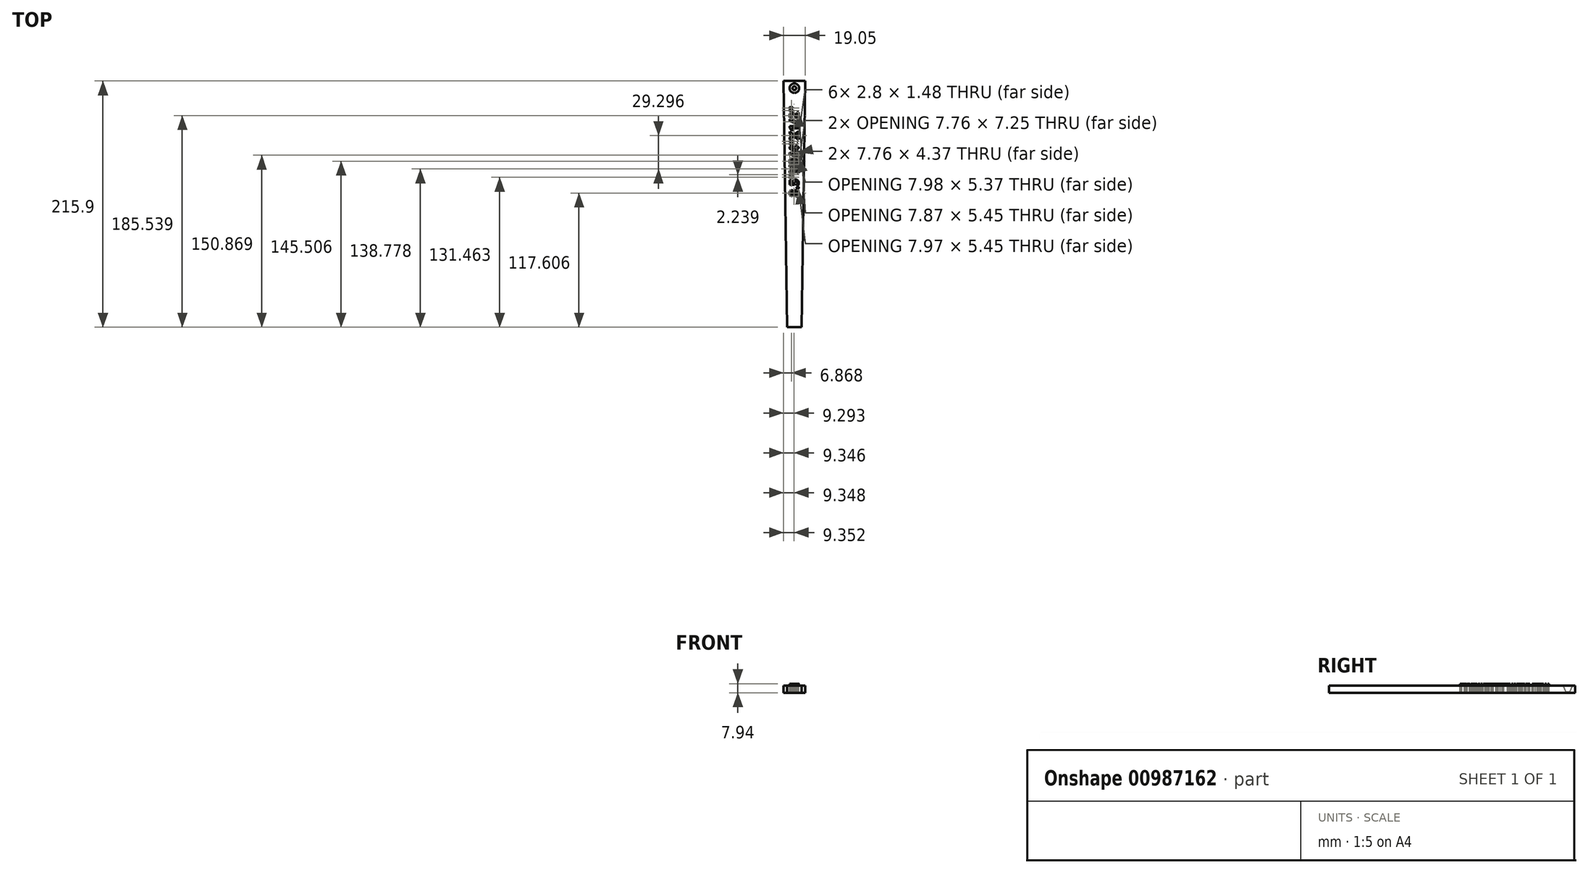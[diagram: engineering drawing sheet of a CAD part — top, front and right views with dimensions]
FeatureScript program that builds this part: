
annotation { "Feature Type Name" : "Feature", "Feature Type Description" : "" }
export const myFeature = defineFeature(function(context is Context, id is Id, definition is map)
    precondition{}
    {
        {
            var Q0;
            Q0=qCreatedBy(makeId("Top.planeOp"),FACE);
            var sketch = newSketch(context, id + "F0", { "sketchPlane" : qUnion([Q0])});
            skLineSegment(sketch, "E0", {"start": v(-44.75, 101.4) * mm, "end": v(-54.28, 101.4) * mm});
            skLineSegment(sketch, "E1", {"start": v(-54.28, 101.4) * mm, "end": v(-44.75, 101.4) * mm});
            skLineSegment(sketch, "E2", {"start": v(-44.75, -114.5) * mm, "end": v(-51.1, -114.5) * mm});
            skLineSegment(sketch, "E3", {"start": v(-51.1, -114.5) * mm, "end": v(-54.28, 101.4) * mm});
            skLineSegment(sketch, "E4.MirrorCS", {"start": v(-44.75, 101.4) * mm, "end": v(-35.23, 101.4) * mm});
            skLineSegment(sketch, "E5.MirrorCS", {"start": v(-38.4, -114.5) * mm, "end": v(-35.23, 101.4) * mm});
            skLineSegment(sketch, "E6.MirrorCS", {"start": v(-44.75, -114.5) * mm, "end": v(-38.4, -114.5) * mm});
            skCircle(sketch, "E7", {"center": v(-44.75, 95.05) * mm, "radius": 1.65 * mm});
            skText(sketch, "E8", { "text": "8.5\"X3/4\"X1/2\"", "fontName": "OpenSans-Bold.ttf"});
            const initialGuessF0  = {"E8": [-0.04105, 0, 0, 1, 0.00783]};
            skSetInitialGuess(sketch, initialGuessF0);
            skSolve(sketch);
        }
        {
            var Q0;
            Q0 = qSketchRegion(id + "F0", true);
            extrude(context, id + "F1", {"entities" : qUnion([Q0]), "oppositeDirection" : true, "depth" : 6.35 * mm, "offsetDistance" : 25.4 * mm});
        }
        {
            var Q0;
            Q0=makeQuery(id+"F0.imprint","IMPRINT",FACE,{"disambiguationData":[TD([[makeQuery(id+"F0.imprint","IMPRINT",EDGE,{"derivedFrom":sQuery(id+"F0.wireOp",EDGE,"E8.sketch_text.stroke-0")}),-1.0]])]});
            var Q1;
            Q1=makeQuery(id+"F0.imprint","IMPRINT",FACE,{"disambiguationData":[TD([[makeQuery(id+"F0.imprint","IMPRINT",EDGE,{"derivedFrom":sQuery(id+"F0.wireOp",EDGE,"E8.sketch_text.stroke-31")}),-1.0]])]});
            var Q2;
            Q2=makeQuery(id+"F0.imprint","IMPRINT",FACE,{"disambiguationData":[TD([[makeQuery(id+"F0.imprint","IMPRINT",EDGE,{"derivedFrom":sQuery(id+"F0.wireOp",EDGE,"E8.sketch_text.stroke-39")}),-1.0]])]});
            var Q3;
            Q3=makeQuery(id+"F0.imprint","IMPRINT",FACE,{"disambiguationData":[TD([[makeQuery(id+"F0.imprint","IMPRINT",EDGE,{"derivedFrom":sQuery(id+"F0.wireOp",EDGE,"E8.sketch_text.stroke-59")}),-1.0]])]});
            var Q4;
            Q4=makeQuery(id+"F0.imprint","IMPRINT",FACE,{"disambiguationData":[TD([[makeQuery(id+"F0.imprint","IMPRINT",EDGE,{"derivedFrom":sQuery(id+"F0.wireOp",EDGE,"E8.sketch_text.stroke-63")}),-1.0]])]});
            var Q5;
            Q5=makeQuery(id+"F0.imprint","IMPRINT",FACE,{"disambiguationData":[TD([[makeQuery(id+"F0.imprint","IMPRINT",EDGE,{"derivedFrom":sQuery(id+"F0.wireOp",EDGE,"E8.sketch_text.stroke-67")}),-1.0]])]});
            var Q6;
            Q6=makeQuery(id+"F0.imprint","IMPRINT",FACE,{"disambiguationData":[TD([[makeQuery(id+"F0.imprint","IMPRINT",EDGE,{"derivedFrom":sQuery(id+"F0.wireOp",EDGE,"E8.sketch_text.stroke-79")}),-1.0]])]});
            var Q7;
            Q7=makeQuery(id+"F0.imprint","IMPRINT",FACE,{"disambiguationData":[TD([[makeQuery(id+"F0.imprint","IMPRINT",EDGE,{"derivedFrom":sQuery(id+"F0.wireOp",EDGE,"E8.sketch_text.stroke-106")}),-1.0]])]});
            var Q8;
            Q8=makeQuery(id+"F0.imprint","IMPRINT",FACE,{"disambiguationData":[TD([[makeQuery(id+"F0.imprint","IMPRINT",EDGE,{"derivedFrom":sQuery(id+"F0.wireOp",EDGE,"E8.sketch_text.stroke-110")}),-1.0]])]});
            var Q9;
            Q9=makeQuery(id+"F0.imprint","IMPRINT",FACE,{"disambiguationData":[TD([[makeQuery(id+"F0.imprint","IMPRINT",EDGE,{"derivedFrom":sQuery(id+"F0.wireOp",EDGE,"E8.sketch_text.stroke-128")}),-1.0]])]});
            var Q10;
            Q10=makeQuery(id+"F0.imprint","IMPRINT",FACE,{"disambiguationData":[TD([[makeQuery(id+"F0.imprint","IMPRINT",EDGE,{"derivedFrom":sQuery(id+"F0.wireOp",EDGE,"E8.sketch_text.stroke-132")}),-1.0]])]});
            var Q11;
            Q11=makeQuery(id+"F0.imprint","IMPRINT",FACE,{"disambiguationData":[TD([[makeQuery(id+"F0.imprint","IMPRINT",EDGE,{"derivedFrom":sQuery(id+"F0.wireOp",EDGE,"E8.sketch_text.stroke-136")}),-1.0]])]});
            var Q12;
            Q12=makeQuery(id+"F0.imprint","IMPRINT",FACE,{"disambiguationData":[TD([[makeQuery(id+"F0.imprint","IMPRINT",EDGE,{"derivedFrom":sQuery(id+"F0.wireOp",EDGE,"E8.sketch_text.stroke-148")}),-1.0]])]});
            var Q13;
            Q13=makeQuery(id+"F0.imprint","IMPRINT",FACE,{"disambiguationData":[TD([[makeQuery(id+"F0.imprint","IMPRINT",EDGE,{"derivedFrom":sQuery(id+"F0.wireOp",EDGE,"E8.sketch_text.stroke-158")}),-1.0]])]});
            var Q14;
            Q14=makeQuery(id+"F0.imprint","IMPRINT",FACE,{"disambiguationData":[TD([[makeQuery(id+"F0.imprint","IMPRINT",EDGE,{"derivedFrom":sQuery(id+"F0.wireOp",EDGE,"E8.sketch_text.stroke-162")}),-1.0]])]});
            var Q15;
            Q15=makeQuery(id+"F0.imprint","IMPRINT",FACE,{"disambiguationData":[TD([[makeQuery(id+"F0.imprint","IMPRINT",EDGE,{"derivedFrom":sQuery(id+"F0.wireOp",EDGE,"E8.sketch_text.stroke-186")}),-1.0]])]});
            var Q16;
            Q16=makeQuery(id+"F0.imprint","IMPRINT",FACE,{"disambiguationData":[TD([[makeQuery(id+"F0.imprint","IMPRINT",EDGE,{"derivedFrom":sQuery(id+"F0.wireOp",EDGE,"E8.sketch_text.stroke-190")}),-1.0]])]});
            extrude(context, id + "F2", {"entities" : qUnion([Q0, Q1, Q2, Q3, Q4, Q5, Q6, Q7, Q8, Q9, Q10, Q11, Q12, Q13, Q14, Q15, Q16]), "depth" : 1.59 * mm, "offsetDistance" : 25.4 * mm});
        }
        {
            var Q0;
            Q0=makeQuery(id+"F1.opExtrude","CAP_EDGE",EDGE,{"disambiguationData":[OSD([sQuery(id+"F0.wireOp",EDGE,"E7")])],"isStart":true});
            chamfer(context, id + "F3", {"entities" : qUnion([Q0]), "chamferType" : ChamferType.TWO_OFFSETS, "width1" : 5.84 * mm, "oppositeDirection" : false, "width2" : 2.54 * mm, "tangentPropagation" : true});
        }
        {
            var Q0;
            Q0=makeQuery(id+"F0.imprint","IMPRINT",FACE,{"disambiguationData":[TD([[makeQuery(id+"F0.imprint","IMPRINT",EDGE,{"derivedFrom":sQuery(id+"F0.wireOp",EDGE,"E8.sketch_text.stroke-23")}),1.0]])]});
            var Q1;
            Q1=makeQuery(id+"F0.imprint","IMPRINT",FACE,{"disambiguationData":[TD([[makeQuery(id+"F0.imprint","IMPRINT",EDGE,{"derivedFrom":sQuery(id+"F0.wireOp",EDGE,"E8.sketch_text.stroke-16")}),1.0]])]});
            var Q2;
            Q2=makeQuery(id+"F0.imprint","IMPRINT",FACE,{"disambiguationData":[TD([[makeQuery(id+"F0.imprint","IMPRINT",EDGE,{"derivedFrom":sQuery(id+"F0.wireOp",EDGE,"E8.sketch_text.stroke-31")}),-1.0]])]});
            var Q3;
            Q3=makeQuery(id+"F0.imprint","IMPRINT",FACE,{"disambiguationData":[TD([[makeQuery(id+"F0.imprint","IMPRINT",EDGE,{"derivedFrom":sQuery(id+"F0.wireOp",EDGE,"E8.sketch_text.stroke-0")}),-1.0]])]});
            var Q4;
            Q4=makeQuery(id+"F0.imprint","IMPRINT",FACE,{"disambiguationData":[TD([[makeQuery(id+"F0.imprint","IMPRINT",EDGE,{"derivedFrom":sQuery(id+"F0.wireOp",EDGE,"E8.sketch_text.stroke-39")}),-1.0]])]});
            var Q5;
            Q5=makeQuery(id+"F0.imprint","IMPRINT",FACE,{"disambiguationData":[TD([[makeQuery(id+"F0.imprint","IMPRINT",EDGE,{"derivedFrom":sQuery(id+"F0.wireOp",EDGE,"E8.sketch_text.stroke-59")}),-1.0]])]});
            var Q6;
            Q6=makeQuery(id+"F0.imprint","IMPRINT",FACE,{"disambiguationData":[TD([[makeQuery(id+"F0.imprint","IMPRINT",EDGE,{"derivedFrom":sQuery(id+"F0.wireOp",EDGE,"E8.sketch_text.stroke-63")}),-1.0]])]});
            var Q7;
            Q7=makeQuery(id+"F0.imprint","IMPRINT",FACE,{"disambiguationData":[TD([[makeQuery(id+"F0.imprint","IMPRINT",EDGE,{"derivedFrom":sQuery(id+"F0.wireOp",EDGE,"E8.sketch_text.stroke-67")}),-1.0]])]});
            var Q8;
            Q8=makeQuery(id+"F0.imprint","IMPRINT",FACE,{"disambiguationData":[TD([[makeQuery(id+"F0.imprint","IMPRINT",EDGE,{"derivedFrom":sQuery(id+"F0.wireOp",EDGE,"E8.sketch_text.stroke-79")}),-1.0]])]});
            var Q9;
            Q9=makeQuery(id+"F0.imprint","IMPRINT",FACE,{"disambiguationData":[TD([[makeQuery(id+"F0.imprint","IMPRINT",EDGE,{"derivedFrom":sQuery(id+"F0.wireOp",EDGE,"E8.sketch_text.stroke-106")}),-1.0]])]});
            var Q10;
            Q10=makeQuery(id+"F0.imprint","IMPRINT",FACE,{"disambiguationData":[TD([[makeQuery(id+"F0.imprint","IMPRINT",EDGE,{"derivedFrom":sQuery(id+"F0.wireOp",EDGE,"E8.sketch_text.stroke-110")}),-1.0]])]});
            var Q11;
            Q11=makeQuery(id+"F0.imprint","IMPRINT",FACE,{"disambiguationData":[TD([[makeQuery(id+"F0.imprint","IMPRINT",EDGE,{"derivedFrom":sQuery(id+"F0.wireOp",EDGE,"E8.sketch_text.stroke-121")}),1.0]])]});
            var Q12;
            Q12=makeQuery(id+"F0.imprint","IMPRINT",FACE,{"disambiguationData":[TD([[makeQuery(id+"F0.imprint","IMPRINT",EDGE,{"derivedFrom":sQuery(id+"F0.wireOp",EDGE,"E8.sketch_text.stroke-128")}),-1.0]])]});
            var Q13;
            Q13=makeQuery(id+"F0.imprint","IMPRINT",FACE,{"disambiguationData":[TD([[makeQuery(id+"F0.imprint","IMPRINT",EDGE,{"derivedFrom":sQuery(id+"F0.wireOp",EDGE,"E8.sketch_text.stroke-132")}),-1.0]])]});
            var Q14;
            Q14=makeQuery(id+"F0.imprint","IMPRINT",FACE,{"disambiguationData":[TD([[makeQuery(id+"F0.imprint","IMPRINT",EDGE,{"derivedFrom":sQuery(id+"F0.wireOp",EDGE,"E8.sketch_text.stroke-136")}),-1.0]])]});
            var Q15;
            Q15=makeQuery(id+"F0.imprint","IMPRINT",FACE,{"disambiguationData":[TD([[makeQuery(id+"F0.imprint","IMPRINT",EDGE,{"derivedFrom":sQuery(id+"F0.wireOp",EDGE,"E8.sketch_text.stroke-148")}),-1.0]])]});
            var Q16;
            Q16=makeQuery(id+"F0.imprint","IMPRINT",FACE,{"disambiguationData":[TD([[makeQuery(id+"F0.imprint","IMPRINT",EDGE,{"derivedFrom":sQuery(id+"F0.wireOp",EDGE,"E8.sketch_text.stroke-158")}),-1.0]])]});
            var Q17;
            Q17=makeQuery(id+"F0.imprint","IMPRINT",FACE,{"disambiguationData":[TD([[makeQuery(id+"F0.imprint","IMPRINT",EDGE,{"derivedFrom":sQuery(id+"F0.wireOp",EDGE,"E8.sketch_text.stroke-162")}),-1.0]])]});
            var Q18;
            Q18=makeQuery(id+"F0.imprint","IMPRINT",FACE,{"disambiguationData":[TD([[makeQuery(id+"F0.imprint","IMPRINT",EDGE,{"derivedFrom":sQuery(id+"F0.wireOp",EDGE,"E8.sketch_text.stroke-190")}),-1.0]])]});
            var Q19;
            Q19=makeQuery(id+"F0.imprint","IMPRINT",FACE,{"disambiguationData":[TD([[makeQuery(id+"F0.imprint","IMPRINT",EDGE,{"derivedFrom":sQuery(id+"F0.wireOp",EDGE,"E8.sketch_text.stroke-186")}),-1.0]])]});
            extrude(context, id + "F4", {"entities" : qUnion([Q0, Q1, Q2, Q3, Q4, Q5, Q6, Q7, Q8, Q9, Q10, Q11, Q12, Q13, Q14, Q15, Q16, Q17, Q18, Q19]), "oppositeDirection" : true, "depth" : 6.35 * mm, "offsetDistance" : 25.4 * mm});
        }
    });
